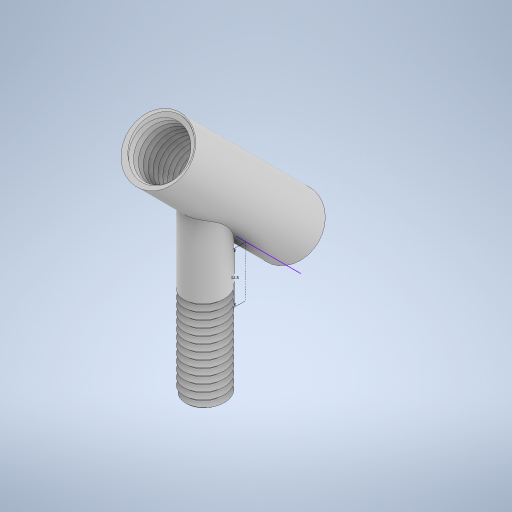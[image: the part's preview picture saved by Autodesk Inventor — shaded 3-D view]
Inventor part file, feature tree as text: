
AUTODESK INVENTOR PART (.ipt)
format: ipt  version: 2024 (Build 280153000, 153)  size: 880,128 bytes
history: native  units: mm
features: sketch x9, plane x5, extrude x3, helix x2, hole x1, chamfer x1
ambient origin geometry x8: Origin, YZ Plane, XZ Plane, XY Plane, X Axis, Y Axis, Z Axis, Center Point
bodies: Solid1 (feature_tree)
feature tree (21):
  extrude  "Extrusion1"  Depth=25.0mm TaperAngle=0.0deg
  plane  "Work Plane1"
  plane  "Work Plane3"
  sketch  "Sketch9"  dims[d16=10.0mm d17=12.5mm]
  plane  "Work Plane4"
  sketch  "Sketch10"  dims[d18=12.5mm d19=45.0deg]
  plane  "Work Plane5"
  extrude  "Extrusion4"  Depth=12.5mm
  hole  "Hole1"  [1 undecoded]
  extrude  "Extrusion5"  Depth=45.0mm TaperAngle=0.0deg
  chamfer  "Chamfer1"  Distance=25.0mm
  sketch  "Sketch14"  dims[d37=1.7mm]
  plane  "Work Plane6"
  helix  "Coil1"  [1 undecoded]
  helix  "Coil2"  [1 undecoded]
  sketch  "Sketch1"  dims[d0=10.0mm d1=25.0mm d2=0.0mm]
  sketch  "Sketch11"  dims[d20=15.0mm d21=45.0mm d22=0.0mm]
  sketch  "Sketch12"  dims[d23=12.0mm]
  sketch  "Sketch13"  dims[d24=12.0mm d25=6.0mm d26=4.0mm d27=2.0mm d28=90.0deg d29=8.0mm d30=20.594885mm d31=25.0mm d32=0.0mm d33=0.8mm d34=2.0mm d35=45.0deg d36=60.0deg]
  sketch  "Sketch15"  dims[d38=2.0mm]
  sketch  "Sketch16"  dims[d39=0.2mm d40=0.0mm d41=1.7mm d42=25.0mm d43=10.0mm d44=0.0mm d45=90.0deg d46=90.0deg d47=0.0mm d48=0.0mm d53=1.7mm d54=60.0deg d55=6.0mm d56=0.2mm d57=1.7mm d58=55.0mm d59=10.0mm d60=0.0mm d61=90.0deg d62=90.0deg d63=0.0mm d64=0.0mm]
note: 3 required parameter values undecoded (feature->parameter linkage not recoverable at this tier; creation-order binding heuristic only, values carry confidence <= 0.55)
